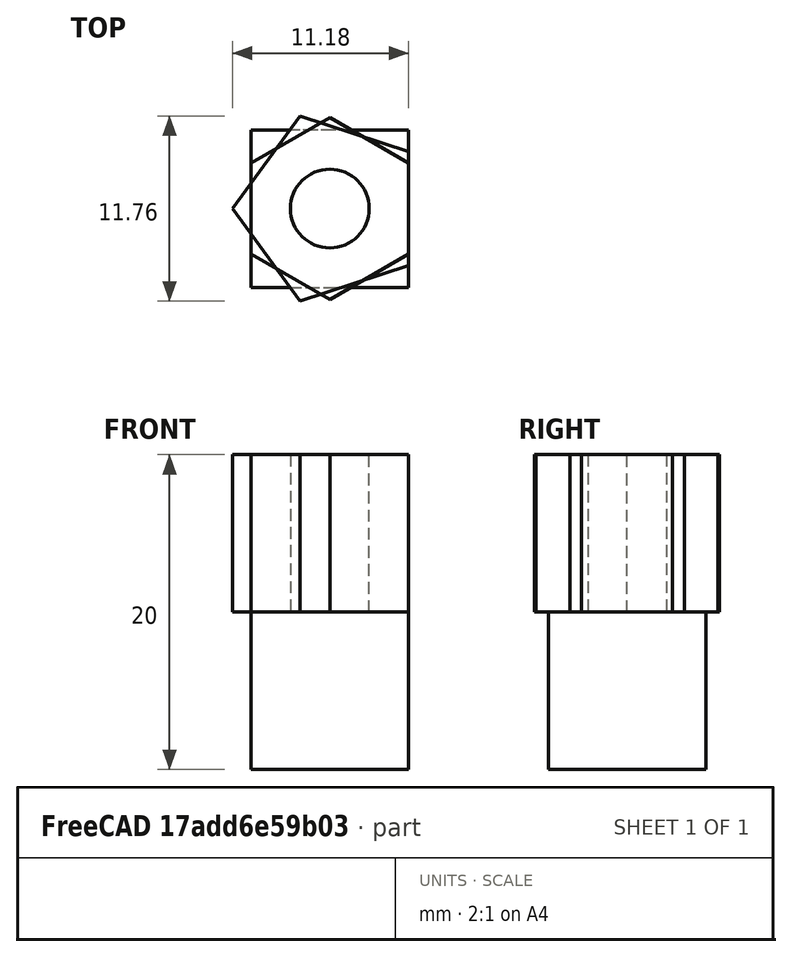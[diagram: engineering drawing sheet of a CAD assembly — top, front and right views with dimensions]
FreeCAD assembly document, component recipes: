
FREECAD ASSEMBLY — COMPONENT RECIPES ("xchg-components-c")

This assembly document has 6 components, labeled P0..P5 below (a component is one placed body or linked part). 6 of them carry a construction recipe — the FreeCAD feature program that regenerates the part from scratch, quoted from this document or its linked companion documents; the rest are supplied as boundary geometry only. No exploded tour is included for this assembly.
COMPONENT P0 — recipe-attached ("Cube 000", modeled in this document).
Construction recipe (the document's own serialized feature program — sketch geometry with constraints, then the solid features built on it; lengths are millimeters unless a unit is written):

FEATURE [Sketcher::SketchObject] Sketch001
  MapMode = 5
  Support = -> [XY_Plane001]
  sketch-geometry (5):
    g0: LineSegment StartX=5 StartY=5 StartZ=0 EndX=-5 EndY=5 EndZ=0
    g1: LineSegment StartX=-5 StartY=5 StartZ=0 EndX=-5 EndY=-5 EndZ=0
    g2: LineSegment StartX=-5 StartY=-5 StartZ=0 EndX=5 EndY=-5 EndZ=0
    g3: LineSegment StartX=5 StartY=-5 StartZ=0 EndX=5 EndY=5 EndZ=0
    g4: Circle [constr] CenterX=0 CenterY=0 CenterZ=0 NormalX=0 NormalY=0 NormalZ=1 AngleXU=0 Radius=7.07107
  constraints (14):
    c: Coincident(g0,g1)
    c: Coincident(g1,g2)
    c: Coincident(g2,g3)
    c: Coincident(g3,g0)
    c: Equal(g0,g1)
    c: Equal(g0,g2)
    c: Equal(g0,g3)
    c: PointOnObject(g0,g4)
    c: PointOnObject(g1,g4)
    c: PointOnObject(g2,g4)
    c: PointOnObject(g3,g4)
    c: Coincident(g4,g-1)
    c: Horizontal(g0)
    c: Distance(g2) = 10
FEATURE [PartDesign::Pad] Pad001
  ClaimChildren = false
  Length = 10
  Length2 = 100
  Profile = -> Sketch001
  Type = 0
FEATURE [PartDesign::Body] Body001  label="Cube 000"
  Group = -> [Sketch001,Pad001]
  Origin = -> Origin001
  Placement = pos=(0,0,-10) rot=(0,0,1;0rad)
  Tip = -> Pad001
COMPONENT P1 — recipe-attached ("Pentagon 000", modeled in this document).
Construction recipe (the document's own serialized feature program — sketch geometry with constraints, then the solid features built on it; lengths are millimeters unless a unit is written):

FEATURE [Sketcher::SketchObject] Sketch002
  MapMode = 5
  Support = -> [XY_Plane002]
  sketch-geometry (6):
    g0: LineSegment StartX=-6.18034 StartY=0 StartZ=0 EndX=-1.90983 EndY=-5.87785 EndZ=0
    g1: LineSegment StartX=-1.90983 StartY=-5.87785 StartZ=0 EndX=5 EndY=-3.63271 EndZ=0
    g2: LineSegment StartX=5 StartY=-3.63271 StartZ=0 EndX=5 EndY=3.63271 EndZ=0
    g3: LineSegment StartX=5 StartY=3.63271 StartZ=0 EndX=-1.90983 EndY=5.87785 EndZ=0
    g4: LineSegment StartX=-1.90983 StartY=5.87785 StartZ=0 EndX=-6.18034 EndY=0 EndZ=0
    g5: Circle [constr] CenterX=0 CenterY=0 CenterZ=0 NormalX=0 NormalY=0 NormalZ=1 AngleXU=0 Radius=6.18034
  constraints (14):
    c: Coincident(g0,g1)
    c: Coincident(g1,g2)
    c: Coincident(g2,g3)
    c: Coincident(g3,g4)
    c: Coincident(g4,g0)
    c: Equal(g0, g1-g4) x4
    c: PointOnObject(g0,g5)
    c: PointOnObject(g1,g5)
    c: PointOnObject(g2,g5)
    c: PointOnObject(g3,g5)
    c: PointOnObject(g4,g5)
    c: Coincident(g5,g-1)
    c: PointOnObject(g4,g-1)
    c: DistanceX(g-1,g1) = 5
FEATURE [PartDesign::Pad] Pad002
  ClaimChildren = false
  Length = 10
  Length2 = 100
  Profile = -> Sketch002
  Type = 0
FEATURE [PartDesign::Body] Body002  label="Pentagon 000"
  Group = -> [Sketch002,Pad002]
  Origin = -> Origin002
  Tip = -> Pad002
COMPONENT P2 — recipe-attached ("Hexagon 000", modeled in this document).
Construction recipe (the document's own serialized feature program — sketch geometry with constraints, then the solid features built on it; lengths are millimeters unless a unit is written):

FEATURE [Sketcher::SketchObject] Sketch003
  MapMode = 5
  Support = -> [XY_Plane003]
  sketch-geometry (7):
    g0: LineSegment StartX=0 StartY=5.7735 StartZ=0 EndX=-5 EndY=2.88675 EndZ=0
    g1: LineSegment StartX=-5 StartY=2.88675 StartZ=0 EndX=-5 EndY=-2.88675 EndZ=0
    g2: LineSegment StartX=-5 StartY=-2.88675 StartZ=0 EndX=0 EndY=-5.7735 EndZ=0
    g3: LineSegment StartX=0 StartY=-5.7735 StartZ=0 EndX=5 EndY=-2.88675 EndZ=0
    g4: LineSegment StartX=5 StartY=-2.88675 StartZ=0 EndX=5 EndY=2.88675 EndZ=0
    g5: LineSegment StartX=5 StartY=2.88675 StartZ=0 EndX=0 EndY=5.7735 EndZ=0
    g6: Circle [constr] CenterX=0 CenterY=0 CenterZ=0 NormalX=0 NormalY=0 NormalZ=1 AngleXU=0 Radius=5.7735
  constraints (16):
    c: Coincident(g0,g1)
    c: Coincident(g1,g2)
    c: Coincident(g2,g3)
    c: Coincident(g3,g4)
    c: Coincident(g4,g5)
    c: Coincident(g5,g0)
    c: Equal(g0, g1-g5) x5
    c: PointOnObject(g0,g6)
    c: PointOnObject(g1,g6)
    c: PointOnObject(g2,g6)
    c: PointOnObject(g3,g6)
    c: PointOnObject(g4,g6)
    c: PointOnObject(g5,g6)
    c: Coincident(g6,g-1)
    c: PointOnObject(g5,g-2)
    c: Distance(g1,g3) = 10
FEATURE [PartDesign::Pad] Pad003
  ClaimChildren = false
  Length = 10
  Length2 = 100
  Profile = -> Sketch003
  Type = 0
FEATURE [PartDesign::Body] Body003  label="Hexagon 000"
  Group = -> [Sketch003,Pad003]
  Origin = -> Origin003
  Tip = -> Pad003
COMPONENT P3 — recipe-attached ("Cylinder 001", modeled in this document).
Construction recipe (the document's own serialized feature program — sketch geometry with constraints, then the solid features built on it; lengths are millimeters unless a unit is written):

FEATURE [Sketcher::SketchObject] Sketch
  MapMode = 5
  Support = -> [XY_Plane]
  sketch-geometry (1):
    g0: Circle CenterX=0 CenterY=0 CenterZ=0 NormalX=0 NormalY=0 NormalZ=1 AngleXU=0 Radius=2.5
  constraints (2):
    c: Coincident(g0,g-1)
    c: Diameter(g0) = 5
FEATURE [PartDesign::Pad] Pad
  ClaimChildren = false
  Length = 10
  Length2 = 100
  Profile = -> Sketch
  Type = 0
FEATURE [PartDesign::Body] Body  label="Cylinder 000"
  Group = -> [Sketch,Pad]
  Origin = -> Origin
  Tip = -> Pad
COMPONENT P4 — same part as P3; its construction recipe is shown at P3.
COMPONENT P5 — same part as P3; its construction recipe is shown at P3.
PROVENANCE & LICENSES
A FreeCAD (.FCStd) document from a public repository crawl; recipes are the document's own serialized feature recipes (and, for linked parts, companion documents' recipes).
License: as declared in the source repository (recorded in the dataset sidecar).
